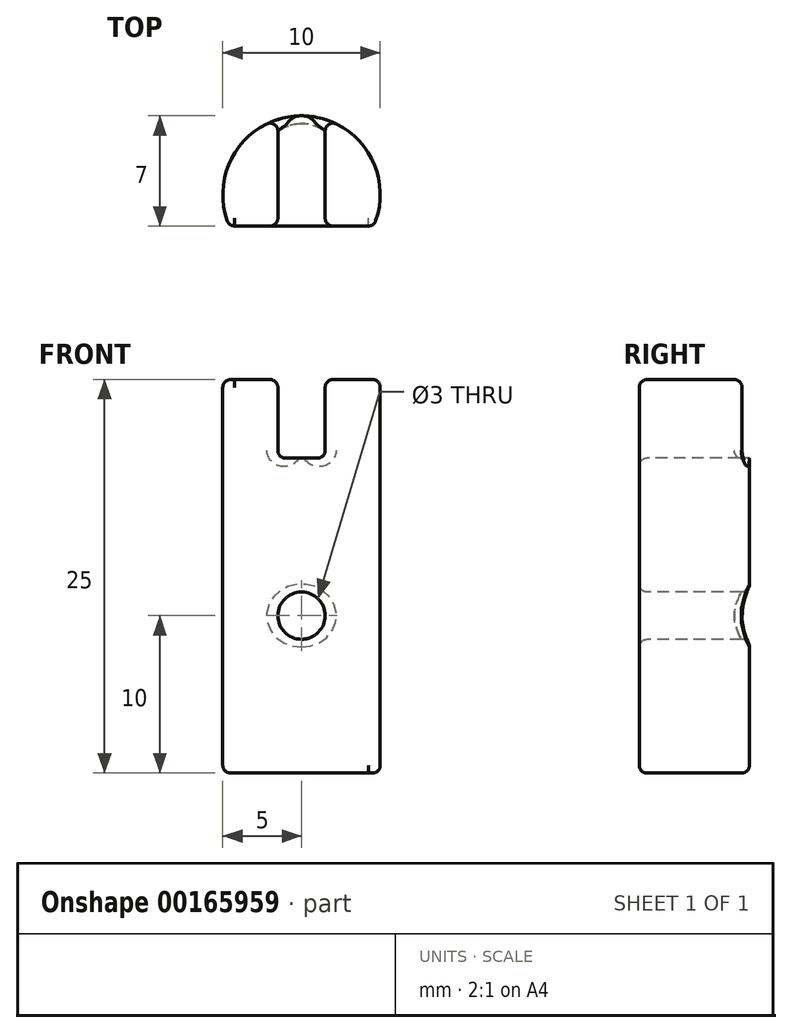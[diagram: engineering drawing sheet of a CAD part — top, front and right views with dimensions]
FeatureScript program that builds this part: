
annotation { "Feature Type Name" : "Feature", "Feature Type Description" : "" }
export const myFeature = defineFeature(function(context is Context, id is Id, definition is map)
    precondition{}
    {
        {
            var Q0;
            Q0=qCreatedBy(makeId("Top.planeOp"),FACE);
            var sketch = newSketch(context, id + "F0", { "sketchPlane" : qUnion([Q0])});
            skCircle(sketch, "E0", {"center": v(0, 0) * mm, "radius": 5 * mm});
            skSolve(sketch);
        }
        {
            var Q0;
            Q0=makeQuery(id+"F0.imprint","IMPRINT",FACE,{"disambiguationData":[TD([[makeQuery(id+"F0.imprint","IMPRINT",EDGE,{"derivedFrom":sQuery(id+"F0.wireOp",EDGE,"E0")}),1.0]])]});
            extrude(context, id + "F1", {"entities" : qUnion([Q0]), "depth" : 25 * mm});
        }
        {
            var Q0;
            Q0=makeQuery(id+"F1.opExtrude","CAP_FACE",FACE,{"disambiguationData":[OSD([sQuery(id+"F0.wireOp",EDGE,"E0")])],"isStart":false});
            var sketch = newSketch(context, id + "F2", { "sketchPlane" : qUnion([Q0])});
            skLineSegment(sketch, "E1", {"start": v(-1.5, 4.77) * mm, "end": v(-1.5, -4.77) * mm});
            skLineSegment(sketch, "E2", {"start": v(1.5, 4.77) * mm, "end": v(1.5, -4.77) * mm});
            skLineSegment(sketch, "E3", {"start": v(-1.5, -4.77) * mm, "end": v(0, -4.77) * mm, "construction": true});
            skLineSegment(sketch, "E4", {"start": v(0, -4.77) * mm, "end": v(1.5, -4.77) * mm, "construction": true});
            skArc(sketch, "E5", {"start": v(-1.5, -4.77) * mm, "mid": v(0, -5) * mm, "end": v(1.5, -4.77) * mm});
            skArc(sketch, "E6.trimOffspring", {"start": v(1.5, 4.77) * mm, "mid": v(0, 5) * mm, "end": v(-1.5, 4.77) * mm});
            skSolve(sketch);
        }
        {
            var Q0;
            Q0 = qSketchRegion(id + "F2", true);
            extrude(context, id + "F3", {"entities" : qUnion([Q0]), "operationType" : NewBodyOperationType.REMOVE, "oppositeDirection" : true, "depth" : 5 * mm});
        }
        {
            var Q0;
            Q0=qCreatedBy(makeId("Front.planeOp"),FACE);
            cPlane(context, id + "F4", {"entities" : qUnion([Q0]), "cplaneType" : CPlaneType.OFFSET, "offset" : 2 * mm, "width" : 150 * mm, "height" : 150 * mm});
        }
        {
            var Q0;
            Q0=qCreatedBy(id+"F4.planeOp",FACE);
            var sketch = newSketch(context, id + "F5", { "sketchPlane" : qUnion([Q0])});
            skLineSegment(sketch, "E7.bottom", {"start": v(-5, 0) * mm, "end": v(5, 0) * mm});
            skLineSegment(sketch, "E7.top", {"start": v(-5, 25) * mm, "end": v(5, 25) * mm});
            skLineSegment(sketch, "E7.left", {"start": v(-5, 0) * mm, "end": v(-5, 25) * mm});
            skLineSegment(sketch, "E7.right", {"start": v(5, 0) * mm, "end": v(5, 25) * mm});
            skSolve(sketch);
        }
        {
            var Q0;
            Q0 = qSketchRegion(id + "F5", true);
            extrude(context, id + "F6", {"entities" : qUnion([Q0]), "operationType" : NewBodyOperationType.REMOVE, "depth" : 8.5 * mm});
        }
        {
            var Q0;
            Q0=makeQuery(id+"F6.boolean.opBoolean","COPY",FACE,{"derivedFrom":makeQuery(id+"F6.opExtrude","CAP_FACE",FACE,{"disambiguationData":[OSD([sQuery(id+"F5.wireOp",EDGE,"E7.bottom"),sQuery(id+"F5.wireOp",EDGE,"E7.top"),sQuery(id+"F5.wireOp",EDGE,"E7.left"),sQuery(id+"F5.wireOp",EDGE,"E7.right")])],"isStart":true})});
            var sketch = newSketch(context, id + "F7", { "sketchPlane" : qUnion([Q0])});
            skCircle(sketch, "E8", {"center": v(0, 10) * mm, "radius": 1.5 * mm});
            skLineSegment(sketch, "E9", {"start": v(0, 10) * mm, "end": v(0, 0) * mm, "construction": true});
            skSolve(sketch);
        }
        {
            var Q0;
            Q0 = qSketchRegion(id + "F7", true);
            extrude(context, id + "F8", {"entities" : qUnion([Q0]), "operationType" : NewBodyOperationType.REMOVE, "endBound" : BoundingType.UP_TO_NEXT, "oppositeDirection" : true, "depth" : 25 * mm});
        }
        {
            var Q0;
            Q0=makeQuery(id+"F3.boolean.opBoolean","COPY",FACE,{"derivedFrom":makeQuery(id+"F3.opExtrude","SWEPT_FACE",FACE,{"disambiguationData":[OSD([sQuery(id+"F2.wireOp",EDGE,"E1")])]})});
            var Q1;
            Q1=makeQuery(id+"F3.boolean.opBoolean","COPY",FACE,{"derivedFrom":makeQuery(id+"F3.opExtrude","SWEPT_FACE",FACE,{"disambiguationData":[OSD([sQuery(id+"F2.wireOp",EDGE,"E2")])]})});
            var Q2;
            {var subQ0=sQuery(id+"F0.wireOp",EDGE,"E0");Q2=makeQuery(id+"F3.boolean.opBoolean","SPLIT",FACE,{"disambiguationData":[TD([makeQuery(id+"F3.opExtrude","SWEPT_FACE",FACE,{"disambiguationData":[OSD([sQuery(id+"F2.wireOp",EDGE,"E2")])]})])],"derivedFrom":makeQuery(id+"F1.opExtrude","CAP_FACE",FACE,{"disambiguationData":[OSD([subQ0])],"isStart":false})});}
            var Q3;
            {var subQ0=sQuery(id+"F0.wireOp",EDGE,"E0");Q3=makeQuery(id+"F3.boolean.opBoolean","SPLIT",FACE,{"disambiguationData":[TD([makeQuery(id+"F3.opExtrude","SWEPT_FACE",FACE,{"disambiguationData":[OSD([sQuery(id+"F2.wireOp",EDGE,"E1")])]})])],"derivedFrom":makeQuery(id+"F1.opExtrude","CAP_FACE",FACE,{"disambiguationData":[OSD([subQ0])],"isStart":false})});}
            var Q4;
            Q4=makeQuery(id+"F8.boolean.opBoolean","COPY",FACE,{"derivedFrom":makeQuery(id+"F8.opExtrude","SWEPT_FACE",FACE,{"disambiguationData":[OSD([sQuery(id+"F7.wireOp",EDGE,"E8")])]})});
            var Q5;
            Q5=makeQuery(id+"F6.boolean.opBoolean","COPY",FACE,{"derivedFrom":makeQuery(id+"F6.opExtrude","CAP_FACE",FACE,{"disambiguationData":[OSD([sQuery(id+"F5.wireOp",EDGE,"E7.bottom"),sQuery(id+"F5.wireOp",EDGE,"E7.top"),sQuery(id+"F5.wireOp",EDGE,"E7.left"),sQuery(id+"F5.wireOp",EDGE,"E7.right")])],"isStart":true})});
            var Q6;
            Q6=makeQuery(id+"F1.opExtrude","CAP_FACE",FACE,{"disambiguationData":[OSD([sQuery(id+"F0.wireOp",EDGE,"E0")])],"isStart":true});
            fillet(context, id + "F9", {"entities" : qUnion([Q0, Q1, Q2, Q3, Q4, Q5, Q6]), "radius" : 0.5 * mm, "tangentPropagation" : true, "allowEdgeOverflow" : false});
        }
    });
